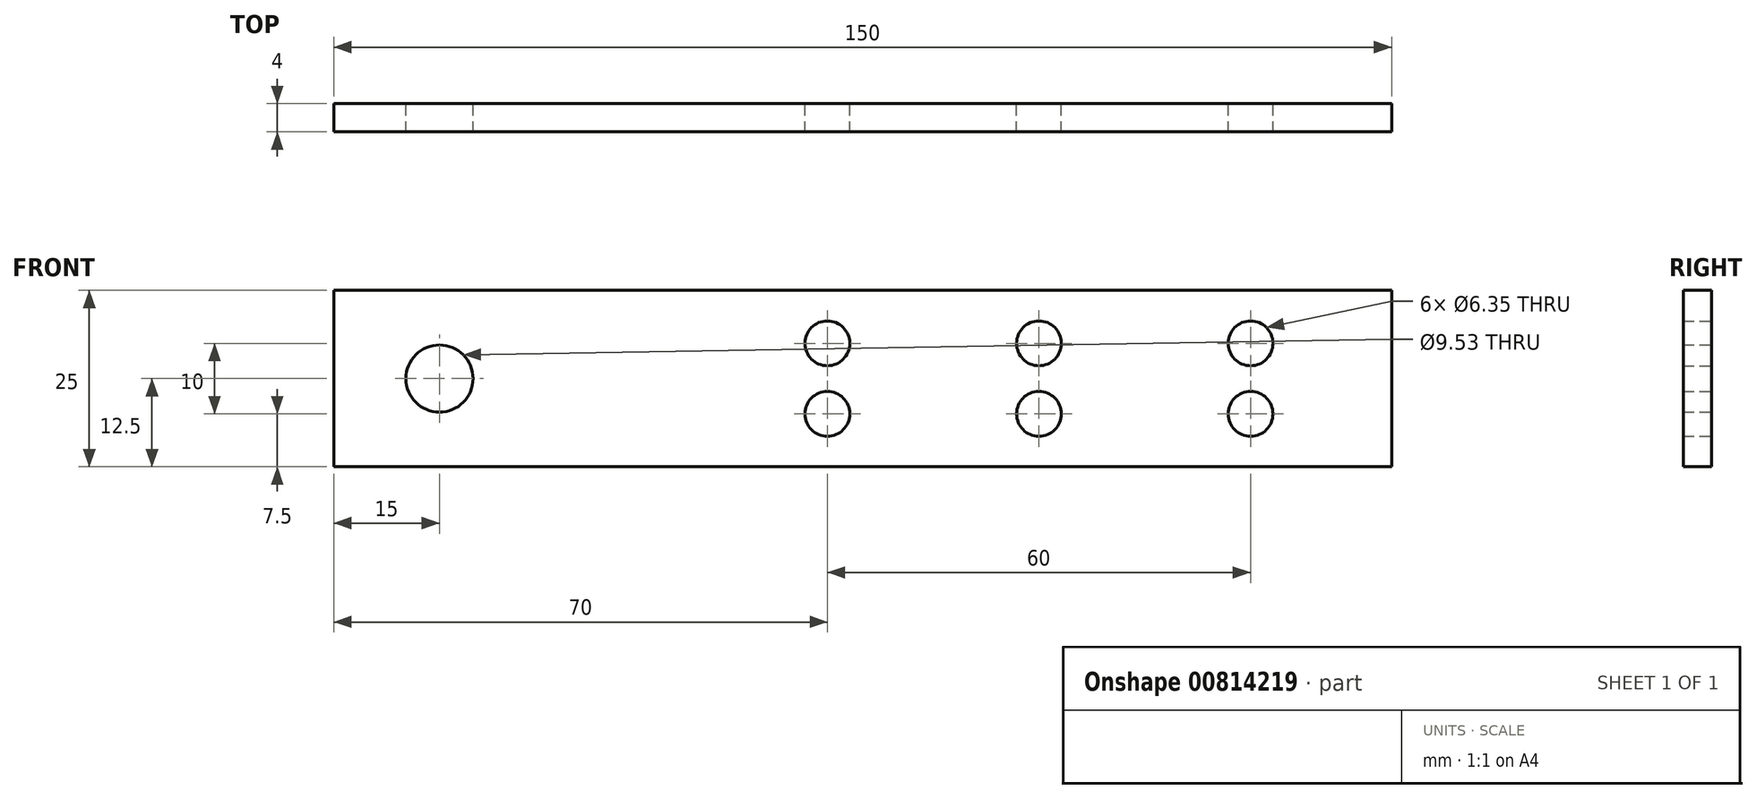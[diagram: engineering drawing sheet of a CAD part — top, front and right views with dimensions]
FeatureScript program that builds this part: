
annotation { "Feature Type Name" : "Feature", "Feature Type Description" : "" }
export const myFeature = defineFeature(function(context is Context, id is Id, definition is map)
    precondition{}
    {
        {
            var Q0;
            Q0=qCreatedBy(makeId("Front.planeOp"),FACE);
            var sketch = newSketch(context, id + "F0", { "sketchPlane" : qUnion([Q0])});
            skLineSegment(sketch, "E0.bottom", {"start": v(0, 0) * mm, "end": v(150, 0) * mm});
            skLineSegment(sketch, "E0.top", {"start": v(0, 25) * mm, "end": v(150, 25) * mm});
            skLineSegment(sketch, "E0.left", {"start": v(0, 0) * mm, "end": v(0, 25) * mm});
            skLineSegment(sketch, "E0.right", {"start": v(150, 0) * mm, "end": v(150, 25) * mm});
            skCircle(sketch, "E1", {"center": v(15, 12.5) * mm, "radius": 4.76 * mm});
            skCircle(sketch, "E2", {"center": v(130, 17.5) * mm, "radius": 3.18 * mm});
            skCircle(sketch, "E3", {"center": v(130, 7.5) * mm, "radius": 3.18 * mm});
            skCircle(sketch, "E4", {"center": v(100, 17.5) * mm, "radius": 3.17 * mm});
            skCircle(sketch, "E5", {"center": v(100, 7.5) * mm, "radius": 3.17 * mm});
            skCircle(sketch, "E6", {"center": v(70, 17.5) * mm, "radius": 3.17 * mm});
            skCircle(sketch, "E7", {"center": v(70, 7.5) * mm, "radius": 3.17 * mm});
            skSolve(sketch);
        }
        {
            var Q0;
            Q0=makeQuery(id+"F0.imprint","IMPRINT",FACE,{"disambiguationData":[TD([[makeQuery(id+"F0.imprint","IMPRINT",EDGE,{"derivedFrom":sQuery(id+"F0.wireOp",EDGE,"E0.bottom")}),1.0]])]});
            extrude(context, id + "F1", {"entities" : qUnion([Q0]), "depth" : 4 * mm, "offsetDistance" : 25 * mm});
        }
    });
